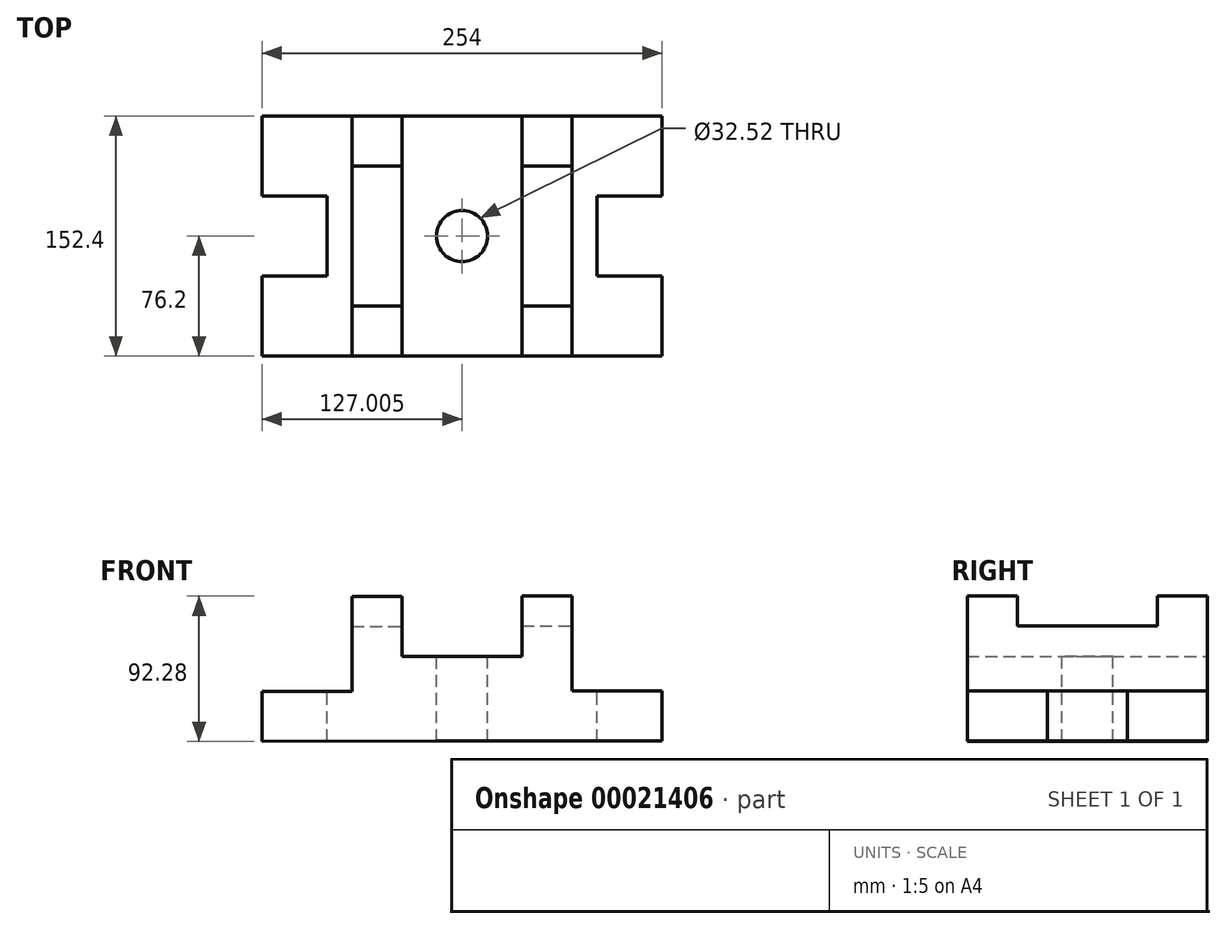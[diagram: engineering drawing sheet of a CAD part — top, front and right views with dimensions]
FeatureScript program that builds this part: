
annotation { "Feature Type Name" : "Feature", "Feature Type Description" : "" }
export const myFeature = defineFeature(function(context is Context, id is Id, definition is map)
    precondition{}
    {
        {
            var Q0;
            Q0=qCreatedBy(makeId("Front.planeOp"),FACE);
            var sketch = newSketch(context, id + "F0", { "sketchPlane" : qUnion([Q0])});
            skLineSegment(sketch, "E0", {"start": v(-36.76, -32.62) * mm, "end": v(90.24, -32.62) * mm});
            skLineSegment(sketch, "E1", {"start": v(90.24, -32.62) * mm, "end": v(90.24, -0.87) * mm});
            skLineSegment(sketch, "E2", {"start": v(90.24, -0.87) * mm, "end": v(33.1, -0.87) * mm});
            skLineSegment(sketch, "E3", {"start": v(33.1, -0.87) * mm, "end": v(33.1, 59.45) * mm});
            skLineSegment(sketch, "E4", {"start": v(33.1, 59.45) * mm, "end": v(1.34, 59.45) * mm});
            skLineSegment(sketch, "E5", {"start": v(1.34, 59.45) * mm, "end": v(1.34, 21.15) * mm});
            skLineSegment(sketch, "E6", {"start": v(1.34, 21.15) * mm, "end": v(-36.76, 21.15) * mm});
            skLineSegment(sketch, "E7", {"start": v(-36.76, 21.15) * mm, "end": v(-74.86, 21.15) * mm});
            skLineSegment(sketch, "E8", {"start": v(-74.86, 21.15) * mm, "end": v(-74.86, 59.34) * mm});
            skLineSegment(sketch, "E9", {"start": v(-74.86, 59.34) * mm, "end": v(-106.6, 59.34) * mm});
            skLineSegment(sketch, "E10", {"start": v(-106.6, 59.34) * mm, "end": v(-106.6, -1.08) * mm});
            skLineSegment(sketch, "E11", {"start": v(-106.6, -1.08) * mm, "end": v(-163.76, -1.08) * mm});
            skLineSegment(sketch, "E12", {"start": v(-163.76, -1.08) * mm, "end": v(-163.76, -32.83) * mm});
            skLineSegment(sketch, "E13", {"start": v(-163.76, -32.83) * mm, "end": v(-36.76, -32.62) * mm});
            skPoint(sketch, "E14.start.orphan", {"position": v(-74.86, -1.08) * mm});
            skSolve(sketch);
        }
        {
            var Q0;
            Q0=makeQuery(id+"F0.imprint","IMPRINT",FACE,{"disambiguationData":[TD([[makeQuery(id+"F0.imprint","IMPRINT",EDGE,{"derivedFrom":sQuery(id+"F0.wireOp",EDGE,"E0")}),1.0]])]});
            extrude(context, id + "F1", {"entities" : qUnion([Q0]), "depth" : 152.4 * mm});
        }
        {
            var Q0;
            Q0=makeQuery(id+"F1.opExtrude","SWEPT_FACE",FACE,{"disambiguationData":[OSD([sQuery(id+"F0.wireOp",EDGE,"E2")])]});
            var sketch = newSketch(context, id + "F2", { "sketchPlane" : qUnion([Q0])});
            skLineSegment(sketch, "E15", {"start": v(90.24, -101.6) * mm, "end": v(48.97, -101.6) * mm});
            skLineSegment(sketch, "E16", {"start": v(48.97, -101.6) * mm, "end": v(48.97, -50.8) * mm});
            skLineSegment(sketch, "E17", {"start": v(48.97, -50.8) * mm, "end": v(90.24, -50.8) * mm});
            skSolve(sketch);
        }
        {
            var Q0;
            {var subQ2=sQuery(id+"F2.wireOp",EDGE,"E15");Q0=makeQuery(id+"F2.imprint","IMPRINT",FACE,{"disambiguationData":[TD([[makeQuery(id+"F2.imprint","IMPRINT",EDGE,{"derivedFrom":subQ2}),-1.0]])]});}
            extrude(context, id + "F3", {"entities" : qUnion([Q0]), "operationType" : NewBodyOperationType.REMOVE, "oppositeDirection" : true, "depth" : 31.75 * mm});
        }
        {
            var Q0;
            Q0=makeQuery(id+"F1.opExtrude","SWEPT_FACE",FACE,{"disambiguationData":[OSD([sQuery(id+"F0.wireOp",EDGE,"E4")])]});
            var sketch = newSketch(context, id + "F4", { "sketchPlane" : qUnion([Q0])});
            skLineSegment(sketch, "E18", {"start": v(1.34, -120.65) * mm, "end": v(33.1, -120.65) * mm});
            skLineSegment(sketch, "E19", {"start": v(1.34, -31.75) * mm, "end": v(33.1, -31.75) * mm});
            skSolve(sketch);
        }
        {
            var Q0;
            {var subQ3=sQuery(id+"F4.wireOp",EDGE,"E18");Q0=makeQuery(id+"F4.imprint","IMPRINT",FACE,{"disambiguationData":[TD([[makeQuery(id+"F4.imprint","IMPRINT",EDGE,{"derivedFrom":subQ3}),1.0]])]});}
            extrude(context, id + "F5", {"entities" : qUnion([Q0]), "operationType" : NewBodyOperationType.REMOVE, "oppositeDirection" : true, "depth" : 19.05 * mm});
        }
        {
            var Q0;
            Q0=makeQuery(id+"F1.opExtrude","SWEPT_FACE",FACE,{"disambiguationData":[OSD([sQuery(id+"F0.wireOp",EDGE,"E11")])]});
            var sketch = newSketch(context, id + "F6", { "sketchPlane" : qUnion([Q0])});
            skLineSegment(sketch, "E20", {"start": v(-163.76, -50.8) * mm, "end": v(-122.48, -50.8) * mm});
            skLineSegment(sketch, "E21", {"start": v(-122.48, -50.8) * mm, "end": v(-122.48, -101.6) * mm});
            skLineSegment(sketch, "E22", {"start": v(-122.48, -101.6) * mm, "end": v(-163.76, -101.6) * mm});
            skSolve(sketch);
        }
        {
            var Q0;
            {var subQ2=sQuery(id+"F6.wireOp",EDGE,"E20");Q0=makeQuery(id+"F6.imprint","IMPRINT",FACE,{"disambiguationData":[TD([[makeQuery(id+"F6.imprint","IMPRINT",EDGE,{"derivedFrom":subQ2}),-1.0]])]});}
            extrude(context, id + "F7", {"entities" : qUnion([Q0]), "operationType" : NewBodyOperationType.REMOVE, "oppositeDirection" : true, "depth" : 31.75 * mm});
        }
        {
            var Q0;
            Q0=makeQuery(id+"F1.opExtrude","SWEPT_FACE",FACE,{"disambiguationData":[OSD([sQuery(id+"F0.wireOp",EDGE,"E9")])]});
            var sketch = newSketch(context, id + "F8", { "sketchPlane" : qUnion([Q0])});
            skLineSegment(sketch, "E23", {"start": v(-106.6, -31.75) * mm, "end": v(-74.86, -31.75) * mm});
            skLineSegment(sketch, "E24", {"start": v(-106.6, -120.65) * mm, "end": v(-74.86, -120.65) * mm});
            skSolve(sketch);
        }
        {
            var Q0;
            {var subQ3=sQuery(id+"F8.wireOp",EDGE,"E23");Q0=makeQuery(id+"F8.imprint","IMPRINT",FACE,{"disambiguationData":[TD([[makeQuery(id+"F8.imprint","IMPRINT",EDGE,{"derivedFrom":subQ3}),-1.0]])]});}
            extrude(context, id + "F9", {"entities" : qUnion([Q0]), "operationType" : NewBodyOperationType.REMOVE, "oppositeDirection" : true, "depth" : 19.05 * mm});
        }
        {
            var Q0;
            Q0=makeQuery(id+"F1.opExtrude","SWEPT_FACE",FACE,{"disambiguationData":[OSD([sQuery(id+"F0.wireOp",EDGE,"E6"),sQuery(id+"F0.wireOp",EDGE,"E7")])]});
            var sketch = newSketch(context, id + "F10", { "sketchPlane" : qUnion([Q0])});
            skCircle(sketch, "E25", {"center": v(-36.76, -76.2) * mm, "radius": 16.26 * mm});
            skSolve(sketch);
        }
        {
            var Q0;
            Q0=makeQuery(id+"F10.imprint","IMPRINT",FACE,{"disambiguationData":[TD([[makeQuery(id+"F10.imprint","IMPRINT",EDGE,{"derivedFrom":sQuery(id+"F10.wireOp",EDGE,"E25")}),1.0]])]});
            extrude(context, id + "F11", {"entities" : qUnion([Q0]), "operationType" : NewBodyOperationType.REMOVE, "oppositeDirection" : true, "depth" : 92.07 * mm});
        }
    });
